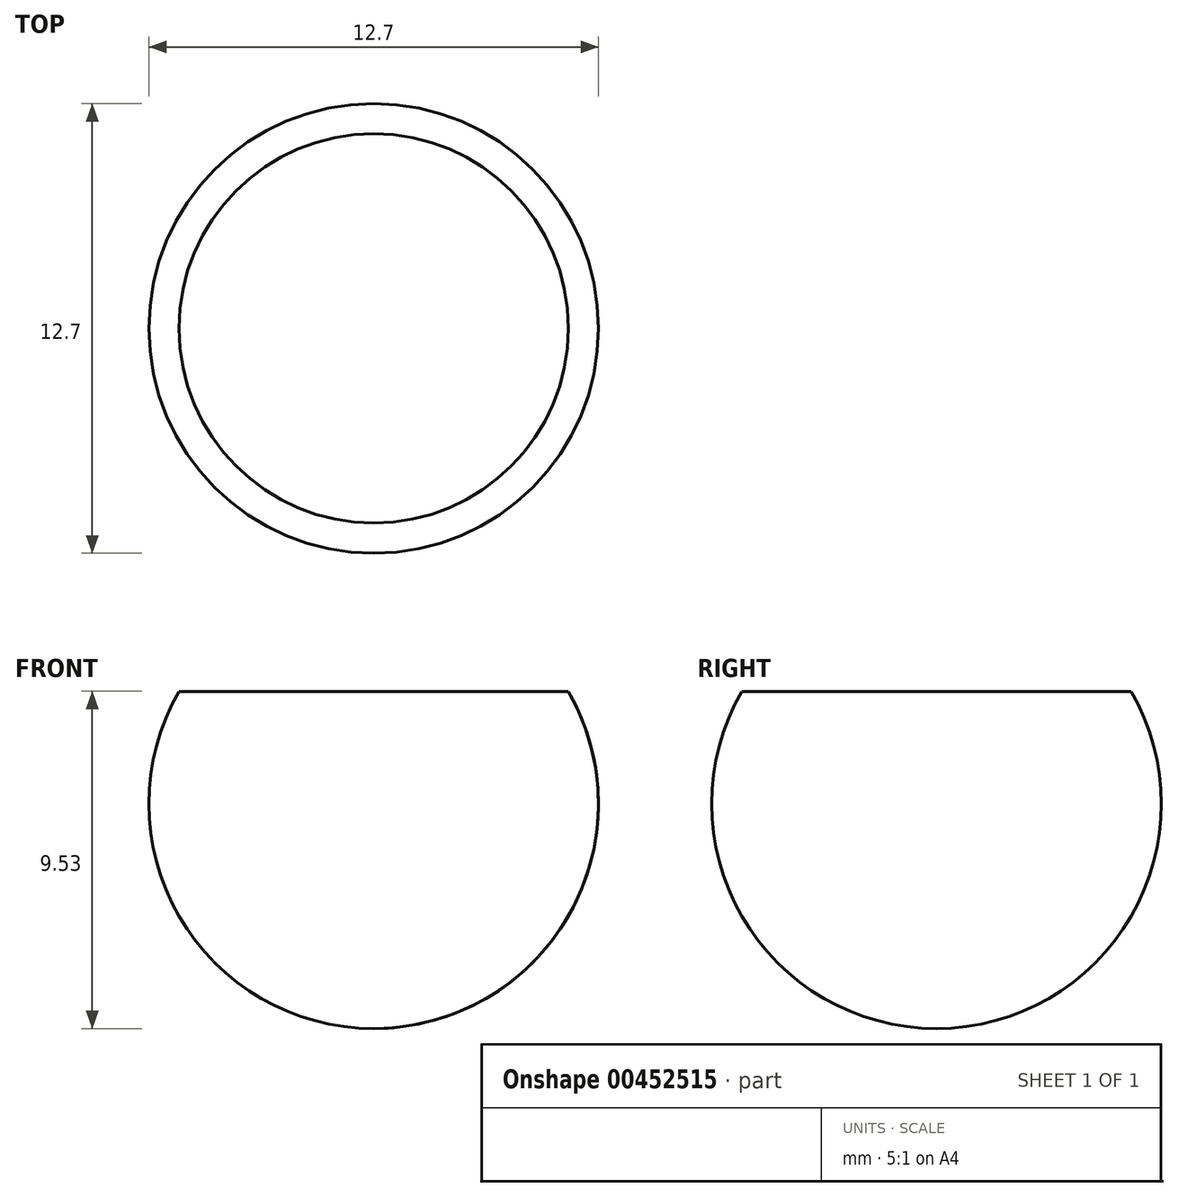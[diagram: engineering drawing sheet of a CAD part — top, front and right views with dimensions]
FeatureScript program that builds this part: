
annotation { "Feature Type Name" : "Feature", "Feature Type Description" : "" }
export const myFeature = defineFeature(function(context is Context, id is Id, definition is map)
    precondition{}
    {
        {
            var Q0;
            Q0=qCreatedBy(makeId("Front.planeOp"),FACE);
            var sketch = newSketch(context, id + "F0", { "sketchPlane" : qUnion([Q0])});
            skLineSegment(sketch, "E0", {"start": v(0, 3.17) * mm, "end": v(0, -6.35) * mm});
            skLineSegment(sketch, "E1", {"start": v(0, 3.18) * mm, "end": v(5.5, 3.18) * mm});
            skArc(sketch, "E2", {"start": v(0, -6.35) * mm, "mid": v(5.5, -3.17) * mm, "end": v(5.5, 3.17) * mm});
            skPoint(sketch, "E3.orphan", {"position": v(-5.5, 3.17) * mm});
            skSolve(sketch);
        }
        {
            var Q0;
            Q0=makeQuery(id+"F0.imprint","IMPRINT",FACE,{"disambiguationData":[TD([[makeQuery(id+"F0.imprint","IMPRINT",EDGE,{"derivedFrom":sQuery(id+"F0.wireOp",EDGE,"E0")}),1.0]])]});
            var Q1;
            Q1=sQuery(id+"F0.wireOp",EDGE,"E0");
            revolve(context, id + "F1", {"entities" : qUnion([Q0]), "axis" : qUnion([Q1]), "revolveType" : RevolveType.FULL});
        }
    });
